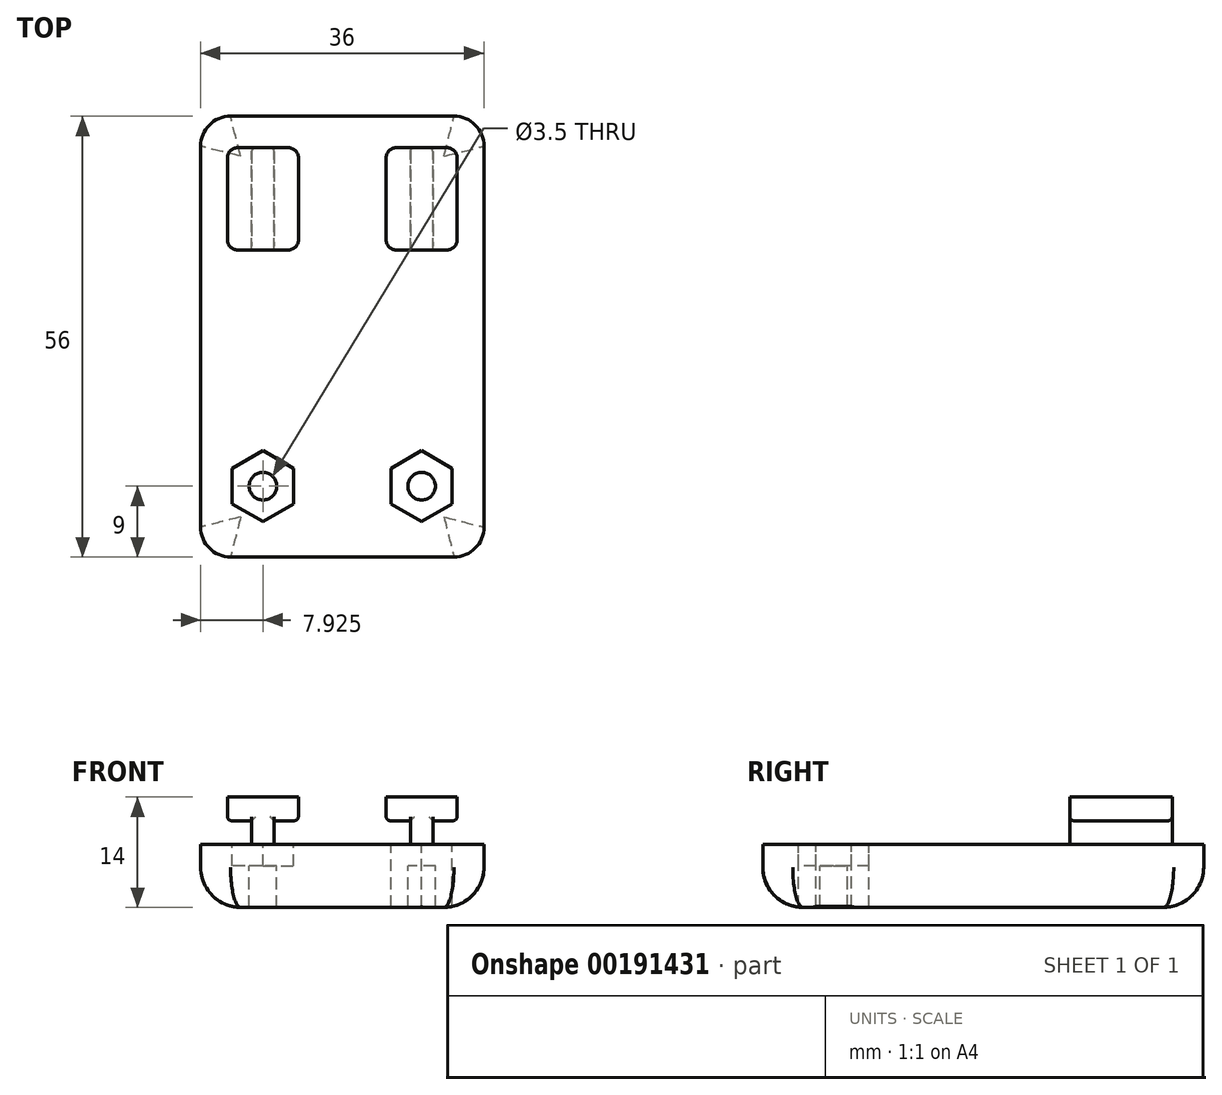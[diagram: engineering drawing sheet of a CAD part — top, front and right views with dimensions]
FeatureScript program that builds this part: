
annotation { "Feature Type Name" : "Feature", "Feature Type Description" : "" }
export const myFeature = defineFeature(function(context is Context, id is Id, definition is map)
    precondition{}
    {
        {
            var Q0;
            Q0=qCreatedBy(makeId("Top.planeOp"),FACE);
            var sketch = newSketch(context, id + "F0", { "sketchPlane" : qUnion([Q0])});
            skLineSegment(sketch, "E0.bottom", {"start": v(14.2, -28) * mm, "end": v(-14.19, -28) * mm});
            skLineSegment(sketch, "E0.top", {"start": v(14.2, 28) * mm, "end": v(-14.2, 28) * mm});
            skLineSegment(sketch, "E0.left", {"start": v(18, -24.2) * mm, "end": v(18, 24.2) * mm});
            skLineSegment(sketch, "E0.right", {"start": v(-18, -24.2) * mm, "end": v(-18, 24.2) * mm});
            skPoint(sketch, "E0.middle", {"position": v(0, 0) * mm});
            skPoint(sketch, "E1.visualSharp", {"position": v(-18, 28) * mm});
            skArc(sketch, "E1.filletArc", {"start": v(-14.2, 28) * mm, "mid": v(-16.88, 26.88) * mm, "end": v(-18, 24.2) * mm});
            skPoint(sketch, "E2.visualSharp", {"position": v(18, 28) * mm});
            skArc(sketch, "E2.filletArc", {"start": v(18, 24.2) * mm, "mid": v(16.88, 26.88) * mm, "end": v(14.2, 28) * mm});
            skPoint(sketch, "E3.visualSharp", {"position": v(18, -28) * mm});
            skArc(sketch, "E3.filletArc", {"start": v(14.2, -28) * mm, "mid": v(16.88, -26.88) * mm, "end": v(18, -24.2) * mm});
            skPoint(sketch, "E4.visualSharp", {"position": v(-18, -28) * mm});
            skArc(sketch, "E4.filletArc", {"start": v(-18, -24.2) * mm, "mid": v(-16.88, -26.88) * mm, "end": v(-14.19, -28) * mm});
            skLineSegment(sketch, "E5", {"start": v(0, 0) * mm, "end": v(0, 28) * mm, "construction": true});
            skLineSegment(sketch, "E6.bottom", {"start": v(-11.5, 24) * mm, "end": v(-8.65, 24) * mm});
            skLineSegment(sketch, "E6.top", {"start": v(-11.5, 11) * mm, "end": v(-8.65, 11) * mm});
            skLineSegment(sketch, "E6.left", {"start": v(-11.5, 24) * mm, "end": v(-11.5, 11) * mm});
            skLineSegment(sketch, "E6.right", {"start": v(-8.65, 24) * mm, "end": v(-8.65, 11) * mm});
            skLineSegment(sketch, "E7.MirrorCS", {"start": v(11.5, 24) * mm, "end": v(8.65, 24) * mm});
            skLineSegment(sketch, "E8.MirrorCS", {"start": v(11.5, 11) * mm, "end": v(8.65, 11) * mm});
            skLineSegment(sketch, "E9.MirrorCS", {"start": v(8.65, 24) * mm, "end": v(8.65, 11) * mm});
            skLineSegment(sketch, "E10.MirrorCS", {"start": v(11.5, 24) * mm, "end": v(11.5, 11) * mm});
            skSolve(sketch);
        }
        {
            var Q0;
            Q0 = qSketchRegion(id + "F0", true);
            var Q1;
            Q1=makeQuery(id+"F0.imprint","IMPRINT",FACE,{"disambiguationData":[TD([[makeQuery(id+"F0.imprint","IMPRINT",EDGE,{"derivedFrom":sQuery(id+"F0.wireOp",EDGE,"E6.bottom")}),-1.0]])]});
            var Q2;
            Q2=makeQuery(id+"F0.imprint","IMPRINT",FACE,{"disambiguationData":[TD([[makeQuery(id+"F0.imprint","IMPRINT",EDGE,{"derivedFrom":sQuery(id+"F0.wireOp",EDGE,"E7.MirrorCS")}),1.0]])]});
            extrude(context, id + "F1", {"entities" : qUnion([Q0, Q1, Q2]), "depth" : 8 * mm});
        }
        {
            var Q0;
            Q0=makeQuery(id+"F0.imprint","IMPRINT",FACE,{"disambiguationData":[TD([[makeQuery(id+"F0.imprint","IMPRINT",EDGE,{"derivedFrom":sQuery(id+"F0.wireOp",EDGE,"E6.bottom")}),-1.0]])]});
            var Q1;
            Q1=makeQuery(id+"F0.imprint","IMPRINT",FACE,{"disambiguationData":[TD([[makeQuery(id+"F0.imprint","IMPRINT",EDGE,{"derivedFrom":sQuery(id+"F0.wireOp",EDGE,"E7.MirrorCS")}),1.0]])]});
            extrude(context, id + "F2", {"entities" : qUnion([Q0, Q1]), "operationType" : NewBodyOperationType.ADD, "depth" : 11 * mm});
        }
        {
            var Q0;
            Q0=makeQuery(id+"F2.opExtrude","CAP_FACE",FACE,{"disambiguationData":[OSD([sQuery(id+"F0.wireOp",EDGE,"E6.bottom"),sQuery(id+"F0.wireOp",EDGE,"E6.top"),sQuery(id+"F0.wireOp",EDGE,"E6.left"),sQuery(id+"F0.wireOp",EDGE,"E6.right")])],"isStart":false});
            var sketch = newSketch(context, id + "F3", { "sketchPlane" : qUnion([Q0])});
            skLineSegment(sketch, "E11.bottom", {"start": v(-6.84, 11) * mm, "end": v(-13.3, 11) * mm});
            skLineSegment(sketch, "E11.top", {"start": v(-6.84, 24) * mm, "end": v(-13.3, 24) * mm});
            skLineSegment(sketch, "E11.left", {"start": v(-5.57, 12.27) * mm, "end": v(-5.57, 22.73) * mm});
            skLineSegment(sketch, "E11.right", {"start": v(-14.58, 12.27) * mm, "end": v(-14.58, 22.73) * mm});
            skPoint(sketch, "E11.middle", {"position": v(-10.08, 17.5) * mm});
            skPoint(sketch, "E11.middle.positionSnap0", {"position": v(-10.08, 24) * mm});
            skPoint(sketch, "E11.middle.positionSnap1", {"position": v(-11.5, 17.5) * mm});
            skPoint(sketch, "E11.centerSnap0", {"position": v(-10.08, 24) * mm});
            skPoint(sketch, "E11.centerSnap1", {"position": v(-11.5, 17.5) * mm});
            skPoint(sketch, "E12.visualSharp", {"position": v(-14.58, 24) * mm});
            skArc(sketch, "E12.filletArc", {"start": v(-13.3, 24) * mm, "mid": v(-14.2, 23.63) * mm, "end": v(-14.57, 22.73) * mm});
            skPoint(sketch, "E13.visualSharp", {"position": v(-5.58, 24) * mm});
            skArc(sketch, "E13.filletArc", {"start": v(-5.57, 22.73) * mm, "mid": v(-5.95, 23.63) * mm, "end": v(-6.84, 24) * mm});
            skPoint(sketch, "E14.visualSharp", {"position": v(-14.58, 11) * mm});
            skArc(sketch, "E14.filletArc", {"start": v(-14.57, 12.27) * mm, "mid": v(-14.2, 11.37) * mm, "end": v(-13.3, 11) * mm});
            skPoint(sketch, "E15.visualSharp", {"position": v(-5.57, 11) * mm});
            skArc(sketch, "E15.filletArc", {"start": v(-6.84, 11) * mm, "mid": v(-5.95, 11.37) * mm, "end": v(-5.57, 12.27) * mm});
            skArc(sketch, "E16.MirrorCS", {"start": v(13.3, 24) * mm, "mid": v(14.2, 23.63) * mm, "end": v(14.58, 22.73) * mm});
            skLineSegment(sketch, "E17.MirrorCS", {"start": v(6.84, 24) * mm, "end": v(13.3, 24) * mm});
            skArc(sketch, "E18.MirrorCS", {"start": v(5.57, 22.73) * mm, "mid": v(5.95, 23.63) * mm, "end": v(6.84, 24) * mm});
            skLineSegment(sketch, "E19.MirrorCS", {"start": v(5.58, 12.27) * mm, "end": v(5.58, 22.73) * mm});
            skArc(sketch, "E20.MirrorCS", {"start": v(6.84, 11) * mm, "mid": v(5.95, 11.37) * mm, "end": v(5.57, 12.27) * mm});
            skLineSegment(sketch, "E21.MirrorCS", {"start": v(6.84, 11) * mm, "end": v(13.3, 11) * mm});
            skArc(sketch, "E22.MirrorCS", {"start": v(14.57, 12.27) * mm, "mid": v(14.2, 11.37) * mm, "end": v(13.3, 11) * mm});
            skLineSegment(sketch, "E23.MirrorCS", {"start": v(14.58, 12.27) * mm, "end": v(14.58, 22.73) * mm});
            skSolve(sketch);
        }
        {
            var Q0;
            Q0 = qSketchRegion(id + "F3", true);
            extrude(context, id + "F4", {"entities" : qUnion([Q0]), "operationType" : NewBodyOperationType.ADD, "depth" : 3 * mm});
        }
        {
            var Q0;
            Q0=makeQuery(id+"F2.opExtrude","SWEPT_EDGE",EDGE,{"disambiguationData":[OSD([sQuery(id+"F0.wireOp",EDGE,"E6.bottom"),sQuery(id+"F0.wireOp",EDGE,"E6.right")])]});
            var Q1;
            Q1=makeQuery(id+"F2.opExtrude","SWEPT_EDGE",EDGE,{"disambiguationData":[OSD([sQuery(id+"F0.wireOp",EDGE,"E6.bottom"),sQuery(id+"F0.wireOp",EDGE,"E6.left")])]});
            var Q2;
            Q2=makeQuery(id+"F2.opExtrude","SWEPT_EDGE",EDGE,{"disambiguationData":[OSD([sQuery(id+"F0.wireOp",EDGE,"E7.MirrorCS"),sQuery(id+"F0.wireOp",EDGE,"E9.MirrorCS")])]});
            var Q3;
            Q3=makeQuery(id+"F2.opExtrude","SWEPT_EDGE",EDGE,{"disambiguationData":[OSD([sQuery(id+"F0.wireOp",EDGE,"E7.MirrorCS"),sQuery(id+"F0.wireOp",EDGE,"E10.MirrorCS")])]});
            var Q4;
            {var subQ1=sQuery(id+"F3.wireOp",EDGE,"E11.top");Q4=makeQuery(id+"F4.boolean.opBoolean","SPLIT",EDGE,{"disambiguationData":[TD([makeQuery(id+"F2.opExtrude","SWEPT_FACE",FACE,{"disambiguationData":[OSD([sQuery(id+"F0.wireOp",EDGE,"E6.right")])]})])],"derivedFrom":makeQuery(id+"F4.opExtrude","CAP_EDGE",EDGE,{"disambiguationData":[OSD([subQ1])],"isStart":true})});}
            var Q5;
            {var subQ1=sQuery(id+"F3.wireOp",EDGE,"E11.top");Q5=makeQuery(id+"F4.boolean.opBoolean","SPLIT",EDGE,{"disambiguationData":[TD([makeQuery(id+"F2.opExtrude","SWEPT_FACE",FACE,{"disambiguationData":[OSD([sQuery(id+"F0.wireOp",EDGE,"E6.left")])]})])],"derivedFrom":makeQuery(id+"F4.opExtrude","CAP_EDGE",EDGE,{"disambiguationData":[OSD([subQ1])],"isStart":true})});}
            var Q6;
            {var subQ0=sQuery(id+"F3.wireOp",EDGE,"E17.MirrorCS");Q6=makeQuery(id+"F4.boolean.opBoolean","SPLIT",EDGE,{"disambiguationData":[TD([makeQuery(id+"F2.opExtrude","SWEPT_FACE",FACE,{"disambiguationData":[OSD([sQuery(id+"F0.wireOp",EDGE,"E10.MirrorCS")])]})])],"derivedFrom":makeQuery(id+"F4.opExtrude","CAP_EDGE",EDGE,{"disambiguationData":[OSD([subQ0])],"isStart":true})});}
            var Q7;
            {var subQ0=sQuery(id+"F3.wireOp",EDGE,"E17.MirrorCS");Q7=makeQuery(id+"F4.boolean.opBoolean","SPLIT",EDGE,{"disambiguationData":[TD([makeQuery(id+"F2.opExtrude","SWEPT_FACE",FACE,{"disambiguationData":[OSD([sQuery(id+"F0.wireOp",EDGE,"E9.MirrorCS")])]})])],"derivedFrom":makeQuery(id+"F4.opExtrude","CAP_EDGE",EDGE,{"disambiguationData":[OSD([subQ0])],"isStart":true})});}
            fillet(context, id + "F5", {"entities" : qUnion([Q0, Q1, Q2, Q3, Q4, Q5, Q6, Q7]), "radius" : 0.5 * mm, "tangentPropagation" : true, "allowEdgeOverflow" : false});
        }
        {
            var Q0;
            Q0=makeQuery(id+"F1.opExtrude","CAP_FACE",FACE,{"disambiguationData":[OSD([sQuery(id+"F0.wireOp",EDGE,"E0.bottom"),sQuery(id+"F0.wireOp",EDGE,"E0.top"),sQuery(id+"F0.wireOp",EDGE,"E0.left"),sQuery(id+"F0.wireOp",EDGE,"E0.right"),sQuery(id+"F0.wireOp",EDGE,"E1.filletArc"),sQuery(id+"F0.wireOp",EDGE,"E2.filletArc"),sQuery(id+"F0.wireOp",EDGE,"E3.filletArc"),sQuery(id+"F0.wireOp",EDGE,"E4.filletArc")])],"isStart":false});
            var sketch = newSketch(context, id + "F6", { "sketchPlane" : qUnion([Q0])});
            skPoint(sketch, "E24.centerSnap0", {"position": v(-10.08, 11) * mm});
            skLineSegment(sketch, "E25", {"start": v(-10.08, 11) * mm, "end": v(-10.08, -19) * mm, "construction": true});
            skLineSegment(sketch, "E26", {"start": v(-13.97, -16.75) * mm, "end": v(-13.97, -21.25) * mm});
            skLineSegment(sketch, "E27.1.0", {"start": v(-13.97, -21.25) * mm, "end": v(-10.08, -23.5) * mm});
            skLineSegment(sketch, "E27.2.0", {"start": v(-10.08, -23.5) * mm, "end": v(-6.18, -21.25) * mm});
            skLineSegment(sketch, "E27.3.0", {"start": v(-6.18, -21.25) * mm, "end": v(-6.18, -16.75) * mm});
            skLineSegment(sketch, "E27.4.0", {"start": v(-6.17, -16.75) * mm, "end": v(-10.07, -14.5) * mm});
            skLineSegment(sketch, "E27.5.0", {"start": v(-10.07, -14.5) * mm, "end": v(-13.97, -16.75) * mm});
            skPoint(sketch, "E27.center", {"position": v(-10.08, -19) * mm});
            skPoint(sketch, "E28.orphan", {"position": v(-3.15, -10.5) * mm});
            skPoint(sketch, "E29.orphan", {"position": v(-13.97, -16.7) * mm});
            skPoint(sketch, "E30.orphan", {"position": v(0.75, -20.75) * mm});
            skPoint(sketch, "E31.orphan", {"position": v(-10.03, -14.47) * mm});
            skPoint(sketch, "E32.orphan", {"position": v(-6.18, -29.25) * mm});
            skPoint(sketch, "E33.orphan", {"position": v(-6.13, -16.77) * mm});
            skPoint(sketch, "E34.orphan", {"position": v(-17, -27.5) * mm});
            skPoint(sketch, "E35.orphan", {"position": v(-6.18, -21.3) * mm});
            skPoint(sketch, "E36.orphan", {"position": v(-10.12, -23.53) * mm});
            skPoint(sketch, "E37.orphan", {"position": v(-20.9, -17.25) * mm});
            skPoint(sketch, "E38.orphan", {"position": v(-14.02, -21.23) * mm});
            skPoint(sketch, "E39.orphan", {"position": v(-13.97, -8.75) * mm});
            skCircle(sketch, "E40", {"center": v(-10.08, -19) * mm, "radius": 1.75 * mm});
            skCircle(sketch, "E41.MirrorC", {"center": v(10.08, -19) * mm, "radius": 1.75 * mm});
            skLineSegment(sketch, "E42.MirrorCS", {"start": v(10.07, -14.5) * mm, "end": v(13.97, -16.75) * mm});
            skPoint(sketch, "E43.MirrorP", {"position": v(6.18, -21.3) * mm});
            skLineSegment(sketch, "E44.MirrorCS", {"start": v(6.17, -16.75) * mm, "end": v(10.07, -14.5) * mm});
            skLineSegment(sketch, "E45.MirrorCS", {"start": v(6.18, -21.25) * mm, "end": v(6.18, -16.75) * mm});
            skPoint(sketch, "E46.MirrorP", {"position": v(3.15, -10.5) * mm});
            skPoint(sketch, "E47.MirrorP", {"position": v(13.97, -8.75) * mm});
            skPoint(sketch, "E48.MirrorP", {"position": v(10.03, -14.47) * mm});
            skPoint(sketch, "E49.MirrorP", {"position": v(20.9, -17.25) * mm});
            skPoint(sketch, "E50.MirrorP", {"position": v(6.13, -16.77) * mm});
            skPoint(sketch, "E51.MirrorP", {"position": v(10.12, -23.53) * mm});
            skPoint(sketch, "E52.MirrorP", {"position": v(13.97, -16.7) * mm});
            skPoint(sketch, "E53.MirrorP", {"position": v(14.02, -21.23) * mm});
            skPoint(sketch, "E54.MirrorP", {"position": v(17, -27.5) * mm});
            skPoint(sketch, "E55.MirrorP", {"position": v(6.18, -29.25) * mm});
            skLineSegment(sketch, "E56.MirrorCS", {"start": v(13.97, -16.75) * mm, "end": v(13.97, -21.25) * mm});
            skLineSegment(sketch, "E57.MirrorCS", {"start": v(10.08, -23.5) * mm, "end": v(6.18, -21.25) * mm});
            skLineSegment(sketch, "E58.MirrorCS", {"start": v(13.97, -21.25) * mm, "end": v(10.08, -23.5) * mm});
            skPoint(sketch, "E59.MirrorP", {"position": v(-0.75, -20.75) * mm});
            skSolve(sketch);
        }
        {
            var Q0;
            Q0=makeQuery(id+"F6.imprint","IMPRINT",FACE,{"disambiguationData":[TD([[makeQuery(id+"F6.imprint","IMPRINT",EDGE,{"derivedFrom":sQuery(id+"F6.wireOp",EDGE,"E40")}),1.0]])]});
            var Q1;
            Q1=makeQuery(id+"F6.imprint","IMPRINT",FACE,{"disambiguationData":[TD([[makeQuery(id+"F6.imprint","IMPRINT",EDGE,{"derivedFrom":sQuery(id+"F6.wireOp",EDGE,"E41.MirrorC")}),-1.0]])]});
            extrude(context, id + "F7", {"entities" : qUnion([Q0, Q1]), "operationType" : NewBodyOperationType.REMOVE, "oppositeDirection" : true, "depth" : 25.4 * mm});
        }
        {
            var Q0;
            Q0=makeQuery(id+"F6.imprint","IMPRINT",FACE,{"disambiguationData":[TD([[makeQuery(id+"F6.imprint","IMPRINT",EDGE,{"derivedFrom":sQuery(id+"F6.wireOp",EDGE,"E26")}),1.0]])]});
            var Q1;
            Q1=makeQuery(id+"F6.imprint","IMPRINT",FACE,{"disambiguationData":[TD([[makeQuery(id+"F6.imprint","IMPRINT",EDGE,{"derivedFrom":sQuery(id+"F6.wireOp",EDGE,"E41.MirrorC")}),1.0]])]});
            extrude(context, id + "F8", {"entities" : qUnion([Q0, Q1]), "operationType" : NewBodyOperationType.REMOVE, "oppositeDirection" : true, "depth" : 2.75 * mm});
        }
        {
            var Q0;
            Q0=makeQuery(id+"F1.opExtrude","CAP_EDGE",EDGE,{"disambiguationData":[OSD([sQuery(id+"F0.wireOp",EDGE,"E0.left")])],"isStart":true});
            fillet(context, id + "F9", {"entities" : qUnion([Q0]), "radius" : 5.08 * mm, "tangentPropagation" : true, "allowEdgeOverflow" : false});
        }
    });
